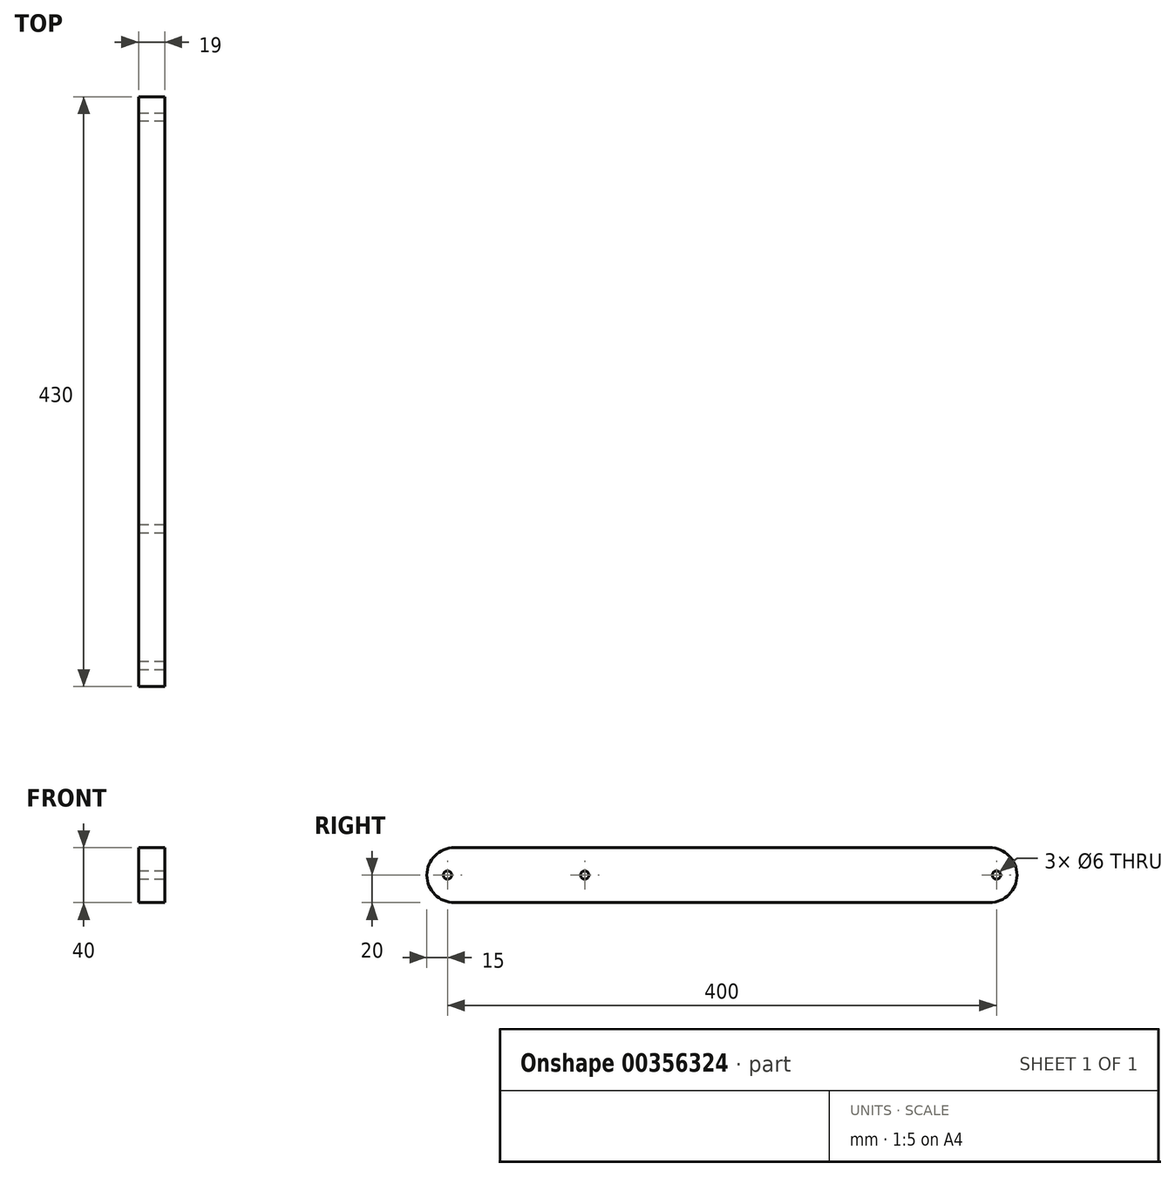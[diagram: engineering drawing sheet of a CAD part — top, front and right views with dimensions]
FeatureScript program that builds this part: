
annotation { "Feature Type Name" : "Feature", "Feature Type Description" : "" }
export const myFeature = defineFeature(function(context is Context, id is Id, definition is map)
    precondition{}
    {
        {
            var Q0;
            Q0=qCreatedBy(makeId("Right.planeOp"),FACE);
            var sketch = newSketch(context, id + "F0", { "sketchPlane" : qUnion([Q0])});
            skCircle(sketch, "E0", {"center": v(0, 0) * mm, "radius": 3 * mm});
            skCircle(sketch, "E1", {"center": v(-400, 0) * mm, "radius": 3 * mm});
            skLineSegment(sketch, "E2.bottom", {"start": v(-415, 20) * mm, "end": v(15, 20) * mm});
            skLineSegment(sketch, "E2.top", {"start": v(-415, -20) * mm, "end": v(15, -20) * mm});
            skLineSegment(sketch, "E2.left", {"start": v(-415, 20) * mm, "end": v(-415, -20) * mm});
            skLineSegment(sketch, "E2.right", {"start": v(15, 20) * mm, "end": v(15, -20) * mm});
            skSolve(sketch);
        }
        {
            var Q0;
            Q0=qSketchRegion(id+"F0",true);
            extrude(context, id + "F1", {"entities" : qUnion([Q0]), "depth" : 19 * mm});
        }
        {
            var Q0;
            Q0=makeQuery(id+"F1.opExtrude","SWEPT_EDGE",EDGE,{"disambiguationData":[OSD([sQuery(id+"F0.wireOp",EDGE,"E2.bottom"),sQuery(id+"F0.wireOp",EDGE,"E2.right")])]});
            var Q1;
            Q1=makeQuery(id+"F1.opExtrude","SWEPT_EDGE",EDGE,{"disambiguationData":[OSD([sQuery(id+"F0.wireOp",EDGE,"E2.top"),sQuery(id+"F0.wireOp",EDGE,"E2.right")])]});
            var Q2;
            Q2=makeQuery(id+"F1.opExtrude","SWEPT_EDGE",EDGE,{"disambiguationData":[OSD([sQuery(id+"F0.wireOp",EDGE,"E2.bottom"),sQuery(id+"F0.wireOp",EDGE,"E2.left")])]});
            var Q3;
            Q3=makeQuery(id+"F1.opExtrude","SWEPT_EDGE",EDGE,{"disambiguationData":[OSD([sQuery(id+"F0.wireOp",EDGE,"E2.top"),sQuery(id+"F0.wireOp",EDGE,"E2.left")])]});
            fillet(context, id + "F2", {"entities" : qUnion([Q0, Q1, Q2, Q3]), "radius" : 20 * mm, "tangentPropagation" : true, "allowEdgeOverflow" : false});
        }
        {
            var Q0;
            Q0=makeQuery(id+"F1.opExtrude","CAP_FACE",FACE,{"disambiguationData":[OSD([sQuery(id+"F0.wireOp",EDGE,"E0"),sQuery(id+"F0.wireOp",EDGE,"E1"),sQuery(id+"F0.wireOp",EDGE,"E2.bottom"),sQuery(id+"F0.wireOp",EDGE,"E2.top"),sQuery(id+"F0.wireOp",EDGE,"E2.left"),sQuery(id+"F0.wireOp",EDGE,"E2.right")])],"isStart":false});
            var sketch = newSketch(context, id + "F3", { "sketchPlane" : qUnion([Q0])});
            skCircle(sketch, "E3", {"center": v(-300, 0) * mm, "radius": 3 * mm});
            skSolve(sketch);
        }
        {
            var Q0;
            Q0=qSketchRegion(id+"F3",true);
            extrude(context, id + "F4", {"entities" : qUnion([Q0]), "operationType" : NewBodyOperationType.REMOVE, "endBound" : BoundingType.THROUGH_ALL, "oppositeDirection" : true, "depth" : 25 * mm});
        }
    });
